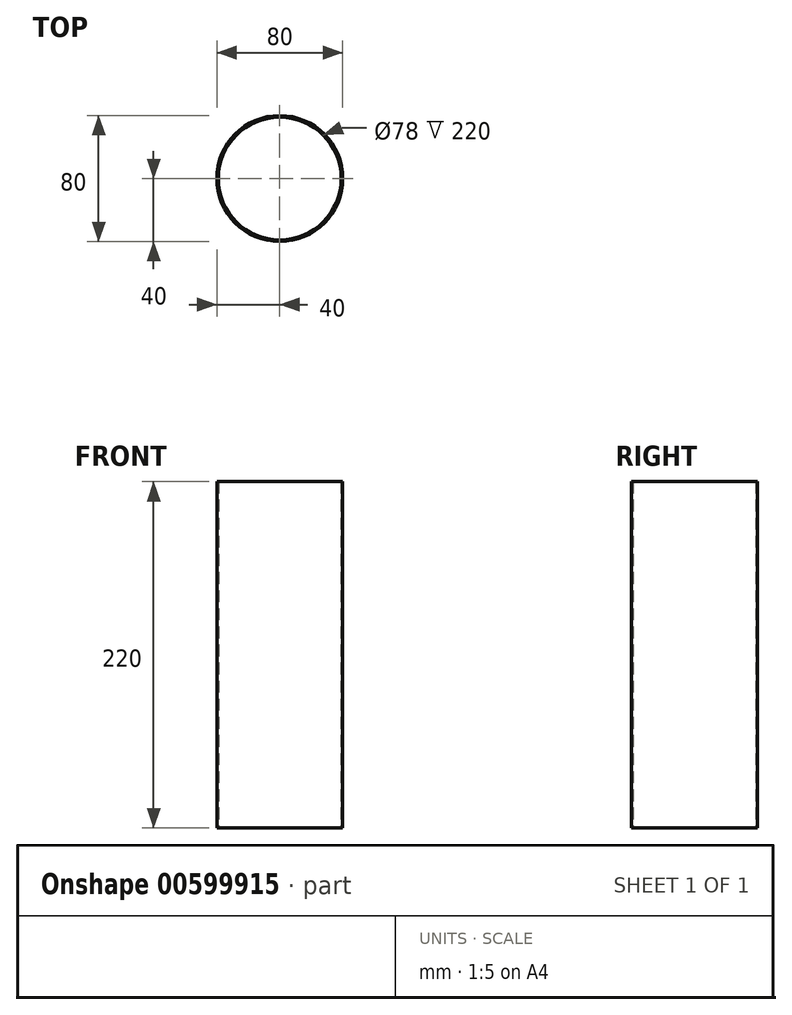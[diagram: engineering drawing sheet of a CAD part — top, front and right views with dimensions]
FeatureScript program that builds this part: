
annotation { "Feature Type Name" : "Feature", "Feature Type Description" : "" }
export const myFeature = defineFeature(function(context is Context, id is Id, definition is map)
    precondition{}
    {
        {
            var Q0;
            Q0=qCreatedBy(makeId("Top.planeOp"),FACE);
            var sketch = newSketch(context, id + "F0", { "sketchPlane" : qUnion([Q0])});
            skCircle(sketch, "E0", {"center": v(0, 0) * mm, "radius": 40 * mm});
            skCircle(sketch, "E1", {"center": v(0, 0) * mm, "radius": 39 * mm});
            skSolve(sketch);
        }
        {
            var Q0;
            Q0=makeQuery(id+"F0.imprint","IMPRINT",FACE,{"disambiguationData":[TD([[makeQuery(id+"F0.imprint","IMPRINT",EDGE,{"derivedFrom":sQuery(id+"F0.wireOp",EDGE,"E0")}),1.0]])]});
            extrude(context, id + "F1", {"entities" : qUnion([Q0]), "depth" : 220 * mm, "offsetDistance" : 25 * mm});
        }
    });
